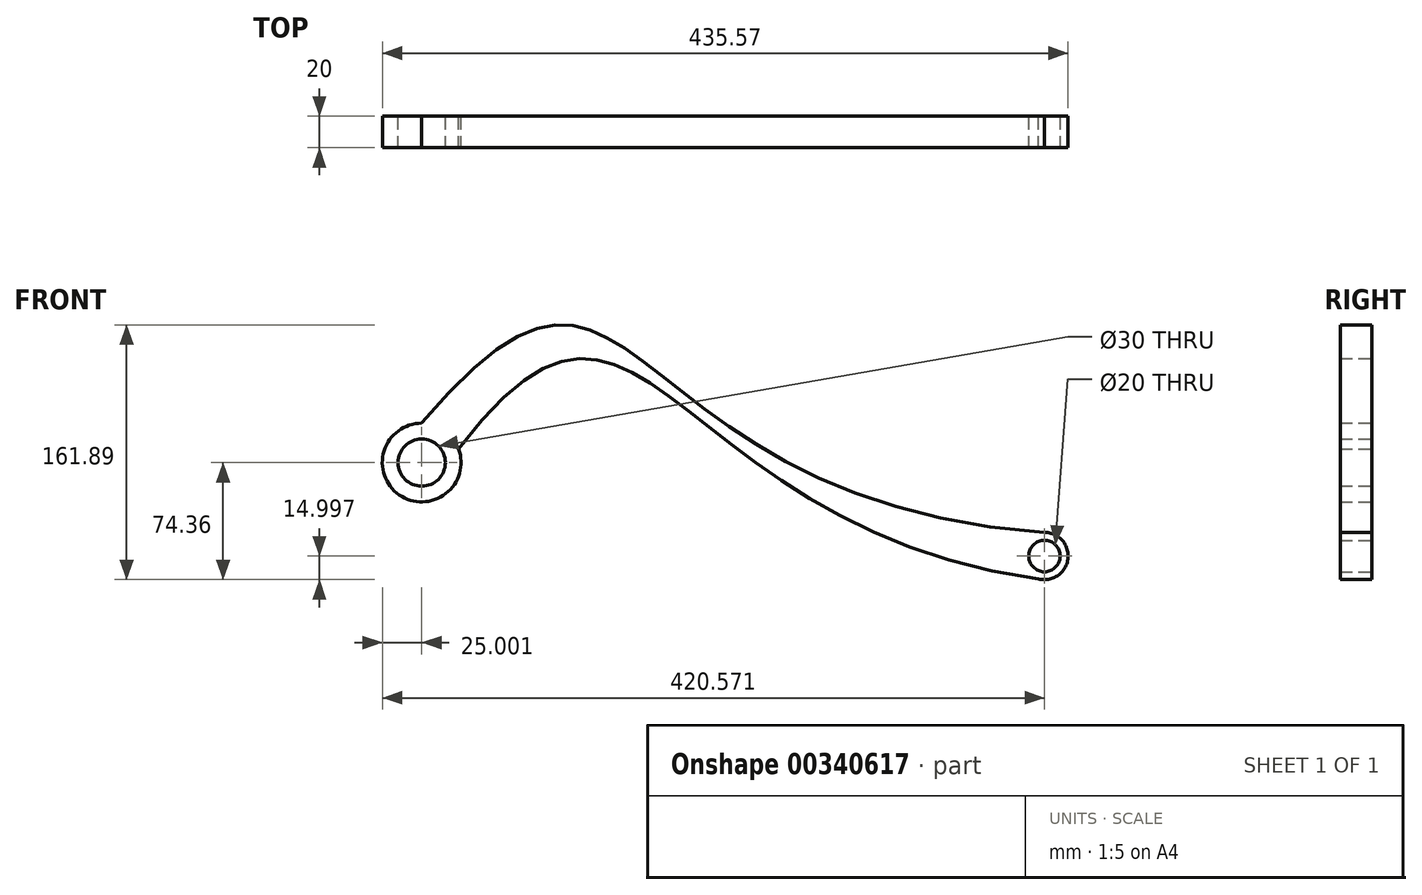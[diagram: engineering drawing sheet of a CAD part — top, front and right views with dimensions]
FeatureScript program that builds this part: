
annotation { "Feature Type Name" : "Feature", "Feature Type Description" : "" }
export const myFeature = defineFeature(function(context is Context, id is Id, definition is map)
    precondition{}
    {
        {
            var Q0;
            Q0=qCreatedBy(makeId("Front.planeOp"),FACE);
            var sketch = newSketch(context, id + "F0", { "sketchPlane" : qUnion([Q0])});
            skCircle(sketch, "E0", {"center": v(-140.59, 0) * mm, "radius": 15 * mm});
            skCircle(sketch, "E1", {"center": v(-140.59, 0) * mm, "radius": 25 * mm});
            skCircle(sketch, "E2", {"center": v(254.98, -59.36) * mm, "radius": 10 * mm});
            skCircle(sketch, "E3", {"center": v(254.98, -59.36) * mm, "radius": 15 * mm});
            skLineSegment(sketch, "E4", {"start": v(-140.59, 0) * mm, "end": v(254.98, -59.36) * mm, "construction": true});
            skPoint(sketch, "E5", {"position": v(-140.59, 25) * mm});
            skPoint(sketch, "E6", {"position": v(-140.59, -25) * mm});
            skPoint(sketch, "E7", {"position": v(254.98, -74.36) * mm});
            skPoint(sketch, "E8", {"position": v(254.98, -44.36) * mm});
            skFitSpline(sketch, "E9", {"points": [v(-140.59, 25) * mm, v(254.98, -44.36) * mm], "startDerivative": vector(421.77, 499.49) * mm, "endDerivative": vector(834.5, -58.09) * mm});
            skFitSpline(sketch, "E10", {"points": [v(-140.59, -25) * mm, v(254.98, -74.36) * mm], "startDerivative": vector(421.77, 649.49) * mm, "endDerivative": vector(764.94, -97.3) * mm});
            skSolve(sketch);
        }
        {
            var Q0;
            Q0=qSketchRegion(id+"F0",true);
            extrude(context, id + "F1", {"entities" : qUnion([Q0]), "depth" : 20 * mm});
        }
    });
